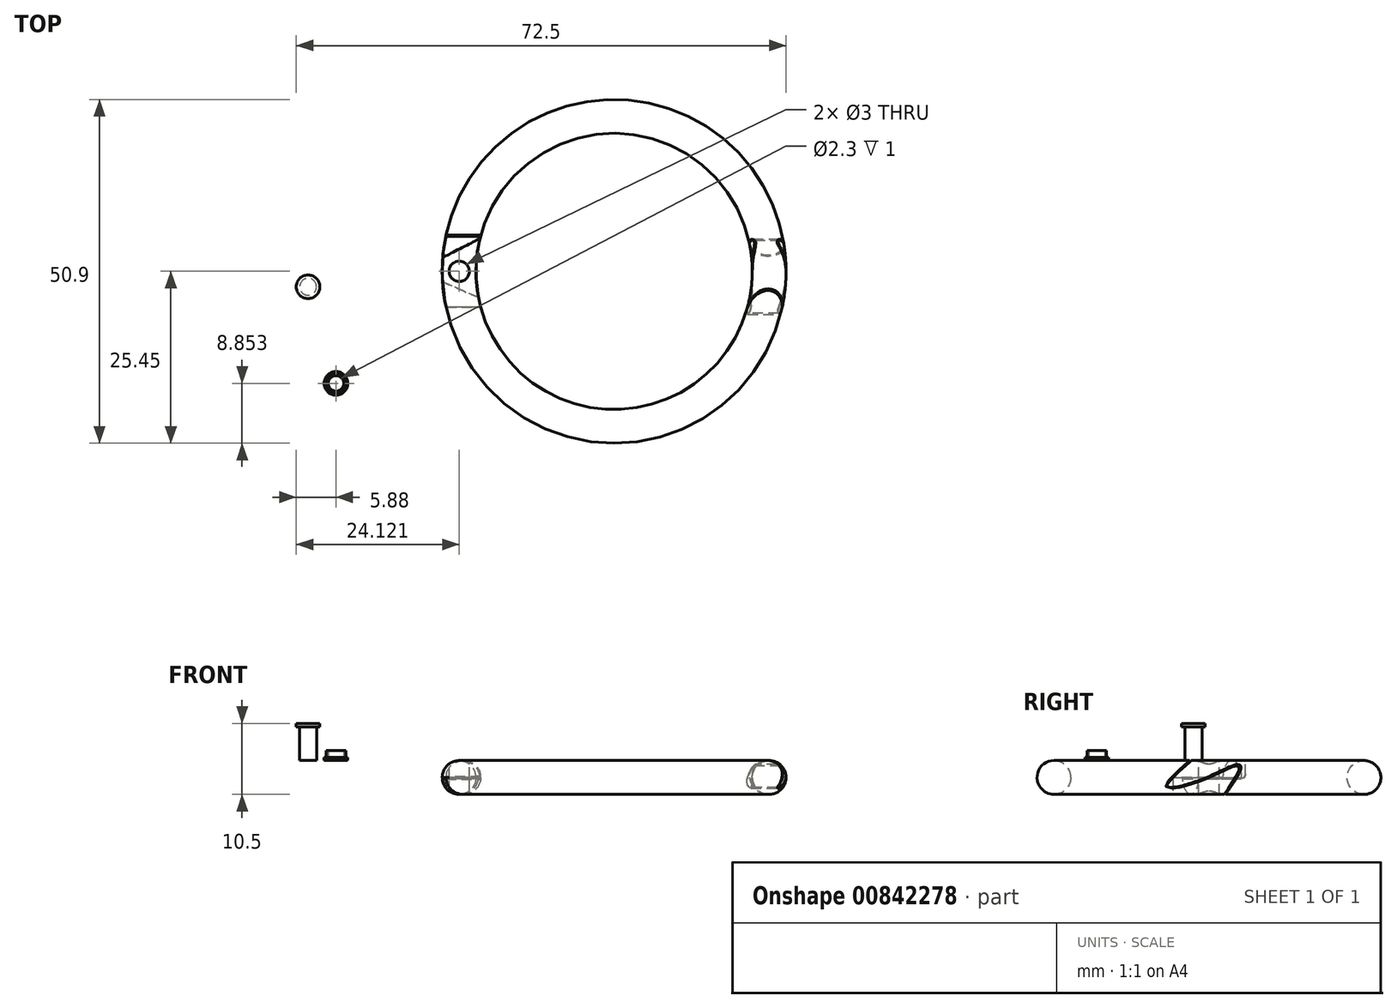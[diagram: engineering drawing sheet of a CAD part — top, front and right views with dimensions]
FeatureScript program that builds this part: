
annotation { "Feature Type Name" : "Feature", "Feature Type Description" : "" }
export const myFeature = defineFeature(function(context is Context, id is Id, definition is map)
    precondition{}
    {
        {
            var Q0;
            Q0=qCreatedBy(makeId("Right.planeOp"),FACE);
            var sketch = newSketch(context, id + "F0", { "sketchPlane" : qUnion([Q0])});
            skCircle(sketch, "E0", {"center": v(-22.95, 0) * mm, "radius": 2.5 * mm});
            skLineSegment(sketch, "E1", {"start": v(0, 6.45) * mm, "end": v(0, -6.17) * mm});
            skSolve(sketch);
        }
        {
            var Q0;
            Q0=makeQuery(id+"F0.imprint","IMPRINT",FACE,{"disambiguationData":[TD([[makeQuery(id+"F0.imprint","IMPRINT",EDGE,{"derivedFrom":sQuery(id+"F0.wireOp",EDGE,"E0")}),1.0]])]});
            var Q1;
            Q1=sQuery(id+"F0.wireOp",EDGE,"E1");
            revolve(context, id + "F1", {"surfaceOperationType" : NewSurfaceOperationType.NEW, "entities" : qUnion([Q0]), "axis" : qUnion([Q1]), "revolveType" : RevolveType.FULL});
        }
        {
            var Q0;
            Q0=qCreatedBy(makeId("Right.planeOp"),FACE);
            var sketch = newSketch(context, id + "F2", { "sketchPlane" : qUnion([Q0])});
            skFitSpline(sketch, "E2", {"points": [v(-2.81, 2.53) * mm, v(-6.32, -1.41) * mm, v(0, 0) * mm, v(4.58, 1.55) * mm, v(2.31, -2.42) * mm, v(2.25, -2.51) * mm], "startDerivative": vector(-23.87, -21.09) * mm, "endDerivative": vector(-0.57, -0.98) * mm});
            skFitSpline(sketch, "E3.0", {"points": [v(-2.7, 2.4) * mm, v(-3.2, 1.97) * mm, v(-3.95, 1.3) * mm, v(-4.82, 0.5) * mm, v(-5.39, -0.07) * mm, v(-5.76, -0.49) * mm, v(-5.98, -0.78) * mm, v(-6.1, -0.97) * mm, v(-6.18, -1.13) * mm, v(-6.2, -1.25) * mm, v(-6.2, -1.32) * mm, v(-6.18, -1.35) * mm, v(-6.1, -1.4) * mm, v(-5.97, -1.44) * mm, v(-5.77, -1.46) * mm, v(-5.43, -1.46) * mm, v(-4.9, -1.4) * mm, v(-4.14, -1.24) * mm, v(-3.27, -1.01) * mm, v(-2.33, -0.72) * mm, v(-1.35, -0.37) * mm, v(-0.36, 0.01) * mm, v(0.6, 0.44) * mm, v(1.53, 0.87) * mm, v(2.38, 1.28) * mm, v(3.01, 1.56) * mm, v(3.45, 1.74) * mm, v(3.75, 1.85) * mm, v(4.01, 1.92) * mm, v(4.24, 1.96) * mm, v(4.41, 1.95) * mm, v(4.54, 1.9) * mm, v(4.63, 1.84) * mm, v(4.7, 1.75) * mm, v(4.74, 1.6) * mm, v(4.74, 1.42) * mm, v(4.68, 1.18) * mm, v(4.57, 0.9) * mm, v(4.43, 0.6) * mm, v(4.2, 0.16) * mm, v(3.84, -0.43) * mm, v(3.39, -1.14) * mm, v(2.96, -1.78) * mm, v(2.6, -2.29) * mm, v(2.43, -2.53) * mm, v(2.4, -2.58) * mm, v(2.4, -2.59) * mm, v(2.4, -2.6) * mm]});
            skLineSegment(sketch, "E4", {"start": v(-2.7, 2.4) * mm, "end": v(-2.57, 2.53) * mm});
            skLineSegment(sketch, "E5", {"start": v(2.25, -2.51) * mm, "end": v(2.4, -2.6) * mm});
            skLineSegment(sketch, "E6", {"start": v(-2.81, 2.53) * mm, "end": v(-2.57, 2.53) * mm});
            skSolve(sketch);
        }
        {
            var Q0;
            Q0=makeQuery(id+"F2.imprint","IMPRINT",FACE,{"disambiguationData":[TD([[makeQuery(id+"F2.imprint","IMPRINT",EDGE,{"derivedFrom":sQuery(id+"F2.wireOp",EDGE,"E2")}),1.0]])]});
            extrude(context, id + "F3", {"entities" : qUnion([Q0]), "operationType" : NewBodyOperationType.REMOVE, "depth" : 33.3 * mm, "offsetDistance" : 25 * mm});
        }
        {
            var Q0;
            Q0=qCreatedBy(makeId("Right.planeOp"),FACE);
            var sketch = newSketch(context, id + "F4", { "sketchPlane" : qUnion([Q0])});
            skLineSegment(sketch, "E7", {"start": v(5.2, 2.6) * mm, "end": v(5.2, 0.48) * mm});
            skLineSegment(sketch, "E8", {"start": v(4.72, 0) * mm, "end": v(-4.84, 0) * mm});
            skLineSegment(sketch, "E9", {"start": v(-5.33, -0.48) * mm, "end": v(-5.33, -2.76) * mm});
            skPoint(sketch, "E10.visualSharp", {"position": v(5.2, 0) * mm});
            skArc(sketch, "E10.filletArc", {"start": v(4.72, 0) * mm, "mid": v(5.07, 0.14) * mm, "end": v(5.2, 0.48) * mm});
            skPoint(sketch, "E11.visualSharp", {"position": v(-5.33, 0) * mm});
            skArc(sketch, "E11.filletArc", {"start": v(-4.84, 0) * mm, "mid": v(-5.19, -0.14) * mm, "end": v(-5.33, -0.48) * mm});
            skLineSegment(sketch, "E12.0", {"start": v(-5.15, -0.48) * mm, "end": v(-5.15, -2.76) * mm});
            skLineSegment(sketch, "E12.1", {"start": v(5.39, 2.6) * mm, "end": v(5.39, 0.48) * mm});
            skArc(sketch, "E12.2", {"start": v(4.72, -0.18) * mm, "mid": v(5.2, 0.01) * mm, "end": v(5.39, 0.48) * mm});
            skLineSegment(sketch, "E12.3", {"start": v(4.72, -0.18) * mm, "end": v(-4.84, -0.18) * mm});
            skArc(sketch, "E12.4", {"start": v(-4.84, -0.18) * mm, "mid": v(-5.06, -0.27) * mm, "end": v(-5.15, -0.48) * mm});
            skLineSegment(sketch, "E13", {"start": v(5.39, 2.6) * mm, "end": v(5.2, 2.6) * mm});
            skLineSegment(sketch, "E14", {"start": v(-5.15, -2.76) * mm, "end": v(-5.33, -2.76) * mm});
            skSolve(sketch);
        }
        {
            var Q0;
            Q0 = qSketchRegion(id + "F4", true);
            extrude(context, id + "F5", {"entities" : qUnion([Q0]), "operationType" : NewBodyOperationType.REMOVE, "oppositeDirection" : true, "depth" : 27.1 * mm, "offsetDistance" : 25 * mm});
        }
        {
            var Q0;
            Q0=qCreatedBy(makeId("Top.planeOp"),FACE);
            var sketch = newSketch(context, id + "F6", { "sketchPlane" : qUnion([Q0])});
            skLineSegment(sketch, "E15", {"start": v(-25.41, 5.27) * mm, "end": v(-18.99, 5.3) * mm});
            skLineSegment(sketch, "E16", {"start": v(-25.41, 2.03) * mm, "end": v(-25.41, 5.27) * mm});
            skLineSegment(sketch, "E17", {"start": v(-25.41, 2.03) * mm, "end": v(-18.99, 5.3) * mm});
            skSolve(sketch);
        }
        {
            var Q0;
            Q0=makeQuery(id+"F6.imprint","IMPRINT",FACE,{"disambiguationData":[TD([[makeQuery(id+"F6.imprint","IMPRINT",EDGE,{"derivedFrom":sQuery(id+"F6.wireOp",EDGE,"E15")}),-1.0]])]});
            var Q1;
            Q1=sQuery(id+"F6.wireOp",EDGE,"E16");
            var Q2;
            Q2=sQuery(id+"F6.wireOp",EDGE,"E15");
            var Q3;
            Q3=sQuery(id+"F6.wireOp",EDGE,"91smAzIS-dtPq-pZ7n-p9sG-Ed96fPETR0M2");
            var Q4;
            Q4=sQuery(id+"F6.wireOp",EDGE,"4sZmHsLb-T351-tJgk-lnvU-juwcBldN6R3C");
            extrude(context, id + "F7", {"entities" : qUnion([Q0]), "operationType" : NewBodyOperationType.REMOVE, "surfaceEntities" : qUnion([Q1, Q2, Q3, Q4]), "depth" : 25 * mm, "offsetDistance" : 25 * mm});
        }
        {
            var Q0;
            Q0=qCreatedBy(makeId("Top.planeOp"),FACE);
            cPlane(context, id + "F8", {"entities" : qUnion([Q0]), "cplaneType" : CPlaneType.OFFSET, "offset" : 2.5 * mm, "width" : 150 * mm, "height" : 150 * mm});
        }
        {
            var Q0;
            Q0=qCreatedBy(id+"F8.planeOp",FACE);
            var sketch = newSketch(context, id + "F9", { "sketchPlane" : qUnion([Q0])});
            skCircle(sketch, "E18", {"center": v(-22.93, 0) * mm, "radius": 1.25 * mm});
            skSolve(sketch);
        }
        {
            var Q0;
            Q0=sQuery(id+"F9.wireOp",VERTEX,"E18.center");
            var Q1;
            Q1=makeQuery(id+"F5.boolean.opBoolean","SPLIT",BODY,{"disambiguationData":[OD(0.0)],"derivedFrom":makeQuery(id+"F1.opRevolve","SWEPT_BODY",BODY,{"disambiguationData":[OSD([sQuery(id+"F0.wireOp",EDGE,"E0")])]})});
            var Q2;
            Q2=makeQuery(id+"F5.boolean.opBoolean","SPLIT",BODY,{"disambiguationData":[OD(1.0)],"derivedFrom":makeQuery(id+"F1.opRevolve","SWEPT_BODY",BODY,{"disambiguationData":[OSD([sQuery(id+"F0.wireOp",EDGE,"E0")])]})});
            hole(context, id + "F10", {"style" : HoleStyle.SIMPLE, "endStyle" : HoleEndStyle.THROUGH, "holeDiameter" : 3 * mm, "majorDiameter" : 5 * mm, "isTappedThrough" : true, "tappedDepth" : 12 * mm, "tapClearance" : 3, "locations" : qUnion([Q0]), "scope" : qUnion([Q1, Q2])});
        }
        {
            var Q0;
            Q0=qCreatedBy(makeId("Top.planeOp"),FACE);
            var sketch = newSketch(context, id + "F11", { "sketchPlane" : qUnion([Q0])});
            skLineSegment(sketch, "E19", {"start": v(-26.83, -5.27) * mm, "end": v(-16.88, -5.27) * mm});
            skLineSegment(sketch, "E20", {"start": v(-16.88, -5.27) * mm, "end": v(-26.68, -1) * mm});
            skLineSegment(sketch, "E21", {"start": v(-26.68, -1) * mm, "end": v(-26.83, -5.27) * mm});
            skSolve(sketch);
        }
        {
            var Q0;
            Q0=makeQuery(id+"F11.imprint","IMPRINT",FACE,{"disambiguationData":[TD([[makeQuery(id+"F11.imprint","IMPRINT",EDGE,{"derivedFrom":sQuery(id+"F11.wireOp",EDGE,"E19")}),1.0]])]});
            extrude(context, id + "F12", {"entities" : qUnion([Q0]), "operationType" : NewBodyOperationType.REMOVE, "oppositeDirection" : true, "depth" : 25 * mm, "offsetDistance" : 25 * mm});
        }
        {
            var Q0;
            Q0=qCreatedBy(id+"F8.planeOp",FACE);
            var sketch = newSketch(context, id + "F13", { "sketchPlane" : qUnion([Q0])});
            skCircle(sketch, "E22", {"center": v(-45.3, -2.3) * mm, "radius": 1.25 * mm});
            skSolve(sketch);
        }
        {
            var Q0;
            Q0 = qSketchRegion(id + "F13", true);
            extrude(context, id + "F14", {"entities" : qUnion([Q0]), "depth" : 5 * mm, "offsetDistance" : 25 * mm});
        }
        {
            var Q0;
            Q0=makeQuery(id+"F14.opExtrude","CAP_FACE",FACE,{"disambiguationData":[OSD([sQuery(id+"F13.wireOp",EDGE,"E22")])],"isStart":false});
            var sketch = newSketch(context, id + "F15", { "sketchPlane" : qUnion([Q0])});
            skCircle(sketch, "E23", {"center": v(-45.3, -2.3) * mm, "radius": 1.75 * mm});
            skSolve(sketch);
        }
        {
            var Q0;
            Q0 = qSketchRegion(id + "F15", true);
            extrude(context, id + "F16", {"entities" : qUnion([Q0]), "operationType" : NewBodyOperationType.ADD, "depth" : 0.5 * mm, "offsetDistance" : 25 * mm});
        }
        {
            var Q0;
            Q0=qCreatedBy(id+"F8.planeOp",FACE);
            var sketch = newSketch(context, id + "F17", { "sketchPlane" : qUnion([Q0])});
            skCircle(sketch, "E24", {"center": v(-41.17, -16.6) * mm, "radius": 1.75 * mm});
            skSolve(sketch);
        }
        {
            var Q0;
            Q0 = qSketchRegion(id + "F17", true);
            extrude(context, id + "F18", {"entities" : qUnion([Q0]), "depth" : 0.5 * mm, "offsetDistance" : 25 * mm});
        }
        {
            var Q0;
            Q0=makeQuery(id+"F18.opExtrude","CAP_FACE",FACE,{"disambiguationData":[OSD([sQuery(id+"F17.wireOp",EDGE,"E24")])],"isStart":false});
            var sketch = newSketch(context, id + "F19", { "sketchPlane" : qUnion([Q0])});
            skCircle(sketch, "E25", {"center": v(-41.17, -16.6) * mm, "radius": 1.45 * mm});
            skCircle(sketch, "E26.0", {"center": v(-41.17, -16.6) * mm, "radius": 1.15 * mm});
            skSolve(sketch);
        }
        {
            var Q0;
            Q0 = qSketchRegion(id + "F19", true);
            extrude(context, id + "F20", {"entities" : qUnion([Q0]), "operationType" : NewBodyOperationType.ADD, "depth" : 1 * mm, "offsetDistance" : 25 * mm});
        }
    });
